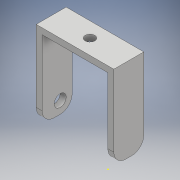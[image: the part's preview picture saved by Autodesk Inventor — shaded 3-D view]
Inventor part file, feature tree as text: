
AUTODESK INVENTOR PART (.ipt)
format: ipt  version: 2018 (Build 220112000, 112)  size: 137,216 bytes
history: native  units: mm
features: sketch x4, extrude x3, other x1, fillet x1
ambient origin geometry x8: Origin, YZ Plane, XZ Plane, XY Plane, X Axis, Y Axis, Z Axis, Center Point
bodies: Solid1 (feature_tree)
feature tree (9):
  other  "Hombro"
  extrude  "Extrusion1"  Depth=10.0mm
  fillet  "Fillet1"  Radius=10.0mm
  extrude  "Extrusion2"  Depth=54.8mm
  sketch  "Sketch3"  dims[d11=8.0mm d12=12.5mm]
  extrude  "Extrusion3"  Depth=12.5mm
  sketch  "Sketch1"  dims[d0=5.0mm d1=70.0mm d2=5.0mm d3=5.0mm d4=25.0mm d5=0.0mm d6=10.0mm d7=10.0mm]
  sketch  "Sketch2"  dims[d8=5.0mm d9=0.0mm d10=54.8mm]
  sketch  "Sketch4"  dims[d13=32.4mm d14=25.0mm d15=64.8mm d16=5.0mm d17=0.0mm]
